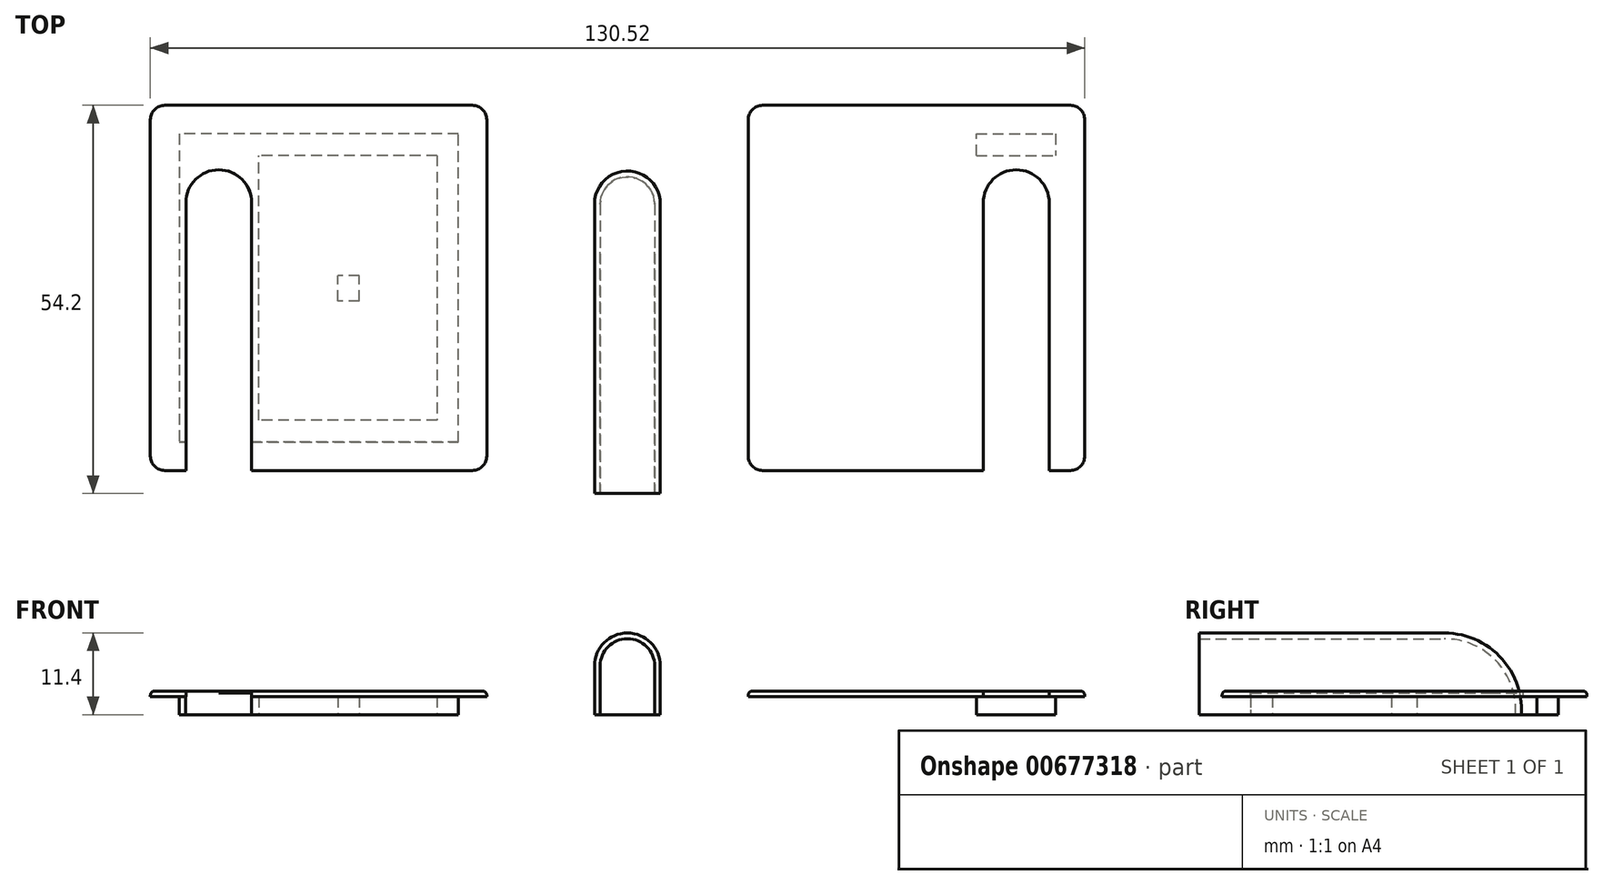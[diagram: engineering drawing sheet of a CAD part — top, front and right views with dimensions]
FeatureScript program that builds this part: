
annotation { "Feature Type Name" : "Feature", "Feature Type Description" : "" }
export const myFeature = defineFeature(function(context is Context, id is Id, definition is map)
    precondition{}
    {
        {
            var Q0;
            Q0=qCreatedBy(makeId("Top.planeOp"),FACE);
            var sketch = newSketch(context, id + "F0", { "sketchPlane" : qUnion([Q0])});
            skLineSegment(sketch, "E0.bottom", {"start": v(-22.21, 21.5) * mm, "end": v(-61.21, 21.5) * mm});
            skLineSegment(sketch, "E0.top", {"start": v(-22.21, -21.5) * mm, "end": v(-61.21, -21.5) * mm});
            skLineSegment(sketch, "E0.left", {"start": v(-22.21, 21.5) * mm, "end": v(-22.21, -21.5) * mm});
            skLineSegment(sketch, "E0.right", {"start": v(-61.21, 21.5) * mm, "end": v(-61.21, -21.5) * mm});
            skPoint(sketch, "E0.middle", {"position": v(-41.71, 0) * mm});
            skPoint(sketch, "E1.middle", {"position": v(-55.71, -10.56) * mm});
            skLineSegment(sketch, "E2", {"start": v(-50, 6.5) * mm, "end": v(0, 6.5) * mm, "construction": true});
            skLineSegment(sketch, "E3.0", {"start": v(0, 16.5) * mm, "end": v(-55.71, 16.5) * mm, "construction": true});
            skPoint(sketch, "E4.oppositeSnap0", {"position": v(-51.12, -5.81) * mm});
            skLineSegment(sketch, "E4.bottom", {"start": v(-60.31, -21.5) * mm, "end": v(-51.12, -21.5) * mm});
            skLineSegment(sketch, "E4.top", {"start": v(-60.28, 16.5) * mm, "end": v(-55.72, 16.5) * mm});
            skLineSegment(sketch, "E4.left", {"start": v(-60.31, -21.5) * mm, "end": v(-60.31, 11.9) * mm});
            skLineSegment(sketch, "E4.right", {"start": v(-51.12, -21.5) * mm, "end": v(-51.12, 11.9) * mm});
            skPoint(sketch, "E5.visualSharp", {"position": v(-51.12, 16.5) * mm});
            skArc(sketch, "E5.filletArc", {"start": v(-51.12, 11.9) * mm, "mid": v(-52.47, 15.15) * mm, "end": v(-55.72, 16.5) * mm});
            skArc(sketch, "E6.filletArc", {"start": v(-55.71, 16.5) * mm, "mid": v(-58.96, 15.15) * mm, "end": v(-60.31, 11.9) * mm});
            skLineSegment(sketch, "E7.0", {"start": v(-50.12, -21.5) * mm, "end": v(-50.12, 21.5) * mm});
            skLineSegment(sketch, "E8.0", {"start": v(-25.21, 18.5) * mm, "end": v(-61.21, 18.5) * mm});
            skLineSegment(sketch, "E8.1", {"start": v(-25.21, 18.5) * mm, "end": v(-25.21, -18.5) * mm});
            skLineSegment(sketch, "E8.2", {"start": v(-25.21, -18.5) * mm, "end": v(-61.21, -18.5) * mm});
            skLineSegment(sketch, "E9.bottom", {"start": v(-50.12, -1.8) * mm, "end": v(-25.21, -1.8) * mm});
            skLineSegment(sketch, "E9.top", {"start": v(-50.12, 1.7) * mm, "end": v(-25.21, 1.7) * mm});
            skLineSegment(sketch, "E9.left", {"start": v(-50.12, -1.8) * mm, "end": v(-50.12, 1.7) * mm});
            skLineSegment(sketch, "E9.right", {"start": v(-25.21, -1.8) * mm, "end": v(-25.21, 1.7) * mm});
            skLineSegment(sketch, "E10.bottom", {"start": v(-39.06, 18.5) * mm, "end": v(-36.06, 18.5) * mm});
            skLineSegment(sketch, "E10.top", {"start": v(-39.06, -18.5) * mm, "end": v(-36.06, -18.5) * mm});
            skLineSegment(sketch, "E10.left", {"start": v(-39.06, 18.5) * mm, "end": v(-39.06, -18.5) * mm});
            skLineSegment(sketch, "E10.right", {"start": v(-36.06, 18.5) * mm, "end": v(-36.06, -18.5) * mm});
            skSolve(sketch);
        }
        {
            var Q0;
            {var subQ5=sQuery(id+"F0.wireOp",EDGE,"DzNkT1zv-doSQ-e9RW-8Sh9-yqjNHehKiuAr.right");Q0=makeQuery(id+"F0.imprint","IMPRINT",FACE,{"disambiguationData":[TD([[makeQuery(id+"F0.imprint","IMPRINT",EDGE,{"derivedFrom":subQ5}),-1.0]])]});}
            var Q1;
            {var subQ0=sQuery(id+"F0.wireOp",EDGE,"DzNkT1zv-doSQ-e9RW-8Sh9-yqjNHehKiuAr.bottom");var subQ1=sQuery(id+"F0.wireOp",EDGE,"ce8b0b9d-27ce-47c4-a76a-4a8f725c700e.0");var subQ2=makeQuery(id+"F0.imprint","INTERSECT",VERTEX,{"derivedFrom":[subQ1,subQ0]});Q1=makeQuery(id+"F0.imprint","IMPRINT",FACE,{"disambiguationData":[TD([[makeQuery(id+"F0.imprint","IMPRINT",EDGE,{"disambiguationData":[TD([[subQ2,-1.0]])],"derivedFrom":subQ1}),-1.0]])]});}
            var Q2;
            {var subQ0=sQuery(id+"F0.wireOp",EDGE,"DzNkT1zv-doSQ-e9RW-8Sh9-yqjNHehKiuAr.bottom");var subQ1=sQuery(id+"F0.wireOp",EDGE,"0b0f2a42-a778-456e-be70-c8d79b466137.0");var subQ2=makeQuery(id+"F0.imprint","INTERSECT",VERTEX,{"derivedFrom":[subQ1,subQ0]});Q2=makeQuery(id+"F0.imprint","IMPRINT",FACE,{"disambiguationData":[TD([[makeQuery(id+"F0.imprint","IMPRINT",EDGE,{"disambiguationData":[TD([[subQ2,-1.0]])],"derivedFrom":subQ1}),1.0]])]});}
            var Q3;
            {var subQ0=sQuery(id+"F0.wireOp",EDGE,"DzNkT1zv-doSQ-e9RW-8Sh9-yqjNHehKiuAr.bottom");var subQ1=sQuery(id+"F0.wireOp",EDGE,"064e6164-91c3-4138-beae-8ed8de8ffb21.0");var subQ2=makeQuery(id+"F0.imprint","INTERSECT",VERTEX,{"derivedFrom":[subQ1,subQ0]});Q3=makeQuery(id+"F0.imprint","IMPRINT",FACE,{"disambiguationData":[TD([[makeQuery(id+"F0.imprint","IMPRINT",EDGE,{"disambiguationData":[TD([[subQ2,-1.0]])],"derivedFrom":subQ1}),1.0]])]});}
            var Q4;
            {var subQ0=sQuery(id+"F0.wireOp",EDGE,"064e6164-91c3-4138-beae-8ed8de8ffb21.0");var subQ1=sQuery(id+"F0.wireOp",EDGE,"dc2ccb20-c1df-4e72-943d-5ddd0a0731c1.2");var subQ2=makeQuery(id+"F0.imprint","INTERSECT",VERTEX,{"derivedFrom":[subQ1,subQ0]});Q4=makeQuery(id+"F0.imprint","IMPRINT",FACE,{"disambiguationData":[TD([[makeQuery(id+"F0.imprint","IMPRINT",EDGE,{"disambiguationData":[TD([[subQ2,1.0]])],"derivedFrom":subQ1}),1.0]])]});}
            var Q5;
            {var subQ0=sQuery(id+"F0.wireOp",EDGE,"ce8b0b9d-27ce-47c4-a76a-4a8f725c700e.0");var subQ1=sQuery(id+"F0.wireOp",EDGE,"dc2ccb20-c1df-4e72-943d-5ddd0a0731c1.2");var subQ2=makeQuery(id+"F0.imprint","INTERSECT",VERTEX,{"derivedFrom":[subQ1,subQ0]});Q5=makeQuery(id+"F0.imprint","IMPRINT",FACE,{"disambiguationData":[TD([[makeQuery(id+"F0.imprint","IMPRINT",EDGE,{"disambiguationData":[TD([[subQ2,-1.0]])],"derivedFrom":subQ1}),1.0]])]});}
            var Q6;
            {var subQ0=sQuery(id+"F0.wireOp",EDGE,"ce8b0b9d-27ce-47c4-a76a-4a8f725c700e.0");var subQ1=sQuery(id+"F0.wireOp",EDGE,"dc2ccb20-c1df-4e72-943d-5ddd0a0731c1.0");var subQ2=makeQuery(id+"F0.imprint","INTERSECT",VERTEX,{"derivedFrom":[subQ1,subQ0]});Q6=makeQuery(id+"F0.imprint","IMPRINT",FACE,{"disambiguationData":[TD([[makeQuery(id+"F0.imprint","IMPRINT",EDGE,{"disambiguationData":[TD([[subQ2,-1.0]])],"derivedFrom":subQ1}),-1.0]])]});}
            var Q7;
            {var subQ0=sQuery(id+"F0.wireOp",EDGE,"064e6164-91c3-4138-beae-8ed8de8ffb21.0");var subQ1=sQuery(id+"F0.wireOp",EDGE,"dc2ccb20-c1df-4e72-943d-5ddd0a0731c1.0");var subQ2=makeQuery(id+"F0.imprint","INTERSECT",VERTEX,{"derivedFrom":[subQ1,subQ0]});Q7=makeQuery(id+"F0.imprint","IMPRINT",FACE,{"disambiguationData":[TD([[makeQuery(id+"F0.imprint","IMPRINT",EDGE,{"disambiguationData":[TD([[subQ2,1.0]])],"derivedFrom":subQ1}),-1.0]])]});}
            var Q8;
            {var subQ20=sQuery(id+"F0.wireOp",EDGE,"E0.bottom");Q8=makeQuery(id+"F0.imprint","IMPRINT",FACE,{"disambiguationData":[TD([[makeQuery(id+"F0.imprint","IMPRINT",EDGE,{"derivedFrom":subQ20}),1.0]])]});}
            extrude(context, id + "F1", {"entities" : qUnion([Q0, Q1, Q2, Q3, Q4, Q5, Q6, Q7, Q8]), "depth" : 2.5 * mm, "offsetDistance" : 25 * mm});
        }
        {
            var Q0;
            Q0=makeQuery(id+"F1.opExtrude","CAP_FACE",FACE,{"disambiguationData":[OSD([sQuery(id+"F0.wireOp",EDGE,"E0.bottom"),sQuery(id+"F0.wireOp",EDGE,"E0.top"),sQuery(id+"F0.wireOp",EDGE,"E0.left"),sQuery(id+"F0.wireOp",EDGE,"E0.right"),sQuery(id+"F0.wireOp",EDGE,"dc2ccb20-c1df-4e72-943d-5ddd0a0731c1.0"),sQuery(id+"F0.wireOp",EDGE,"dc2ccb20-c1df-4e72-943d-5ddd0a0731c1.1"),sQuery(id+"F0.wireOp",EDGE,"dc2ccb20-c1df-4e72-943d-5ddd0a0731c1.2"),sQuery(id+"F0.wireOp",EDGE,"dc2ccb20-c1df-4e72-943d-5ddd0a0731c1.3"),sQuery(id+"F0.wireOp",EDGE,"064e6164-91c3-4138-beae-8ed8de8ffb21.0"),sQuery(id+"F0.wireOp",EDGE,"ce8b0b9d-27ce-47c4-a76a-4a8f725c700e.0"),sQuery(id+"F0.wireOp",EDGE,"0b0f2a42-a778-456e-be70-c8d79b466137.0"),sQuery(id+"F0.wireOp",EDGE,"c18b5a97-83d3-40bf-b302-a28a2e8d01a5.0"),sQuery(id+"F0.wireOp",EDGE,"DzNkT1zv-doSQ-e9RW-8Sh9-yqjNHehKiuAr.bottom"),sQuery(id+"F0.wireOp",EDGE,"DzNkT1zv-doSQ-e9RW-8Sh9-yqjNHehKiuAr.top"),sQuery(id+"F0.wireOp",EDGE,"56cf2d36-3c2d-4065-9a66-2b18e07928f5.0"),sQuery(id+"F0.wireOp",EDGE,"oqrG9gOV-pN6u-iuo7-ISGW-Ieqw6STCVA0x"),sQuery(id+"F0.wireOp",EDGE,"7Q4F9jyW-YGvi-0pui-QKdC-qTxHTYruCEjz")])],"isStart":false});
            var sketch = newSketch(context, id + "F2", { "sketchPlane" : qUnion([Q0])});
            skLineSegment(sketch, "E11.bottom", {"start": v(-20.26, -25.5) * mm, "end": v(-63.26, -25.5) * mm});
            skLineSegment(sketch, "E11.top", {"start": v(-20.26, 25.5) * mm, "end": v(-63.26, 25.5) * mm});
            skLineSegment(sketch, "E11.left", {"start": v(-18.26, -23.5) * mm, "end": v(-18.26, 23.5) * mm});
            skLineSegment(sketch, "E11.right", {"start": v(-65.26, -23.5) * mm, "end": v(-65.26, 23.5) * mm});
            skPoint(sketch, "E11.middle", {"position": v(-41.76, 0) * mm});
            skPoint(sketch, "E11.middle.positionSnap0", {"position": v(-41.76, -1.5) * mm});
            skPoint(sketch, "E11.centerSnap0", {"position": v(-41.76, -1.5) * mm});
            skPoint(sketch, "E12.visualSharp", {"position": v(-65.26, 25.5) * mm});
            skArc(sketch, "E12.filletArc", {"start": v(-63.26, 25.5) * mm, "mid": v(-64.68, 24.91) * mm, "end": v(-65.26, 23.5) * mm});
            skPoint(sketch, "E13.visualSharp", {"position": v(-18.26, 25.5) * mm});
            skArc(sketch, "E13.filletArc", {"start": v(-18.26, 23.5) * mm, "mid": v(-18.85, 24.91) * mm, "end": v(-20.26, 25.5) * mm});
            skPoint(sketch, "E14.visualSharp", {"position": v(-65.26, -25.5) * mm});
            skArc(sketch, "E14.filletArc", {"start": v(-65.26, -23.5) * mm, "mid": v(-64.68, -24.91) * mm, "end": v(-63.26, -25.5) * mm});
            skPoint(sketch, "E15.visualSharp", {"position": v(-18.26, -25.5) * mm});
            skArc(sketch, "E15.filletArc", {"start": v(-20.26, -25.5) * mm, "mid": v(-18.85, -24.91) * mm, "end": v(-18.26, -23.5) * mm});
            skLineSegment(sketch, "E16.bottom", {"start": v(-60.3, -25.5) * mm, "end": v(-51.1, -25.5) * mm});
            skLineSegment(sketch, "E16.top", {"start": v(-60.3, 11.9) * mm, "end": v(-51.1, 11.9) * mm});
            skLineSegment(sketch, "E16.left", {"start": v(-60.3, -25.5) * mm, "end": v(-60.3, 11.9) * mm});
            skLineSegment(sketch, "E16.right", {"start": v(-51.1, -25.5) * mm, "end": v(-51.1, 11.9) * mm});
            skArc(sketch, "E17", {"start": v(-51.1, 11.9) * mm, "mid": v(-55.7, 16.5) * mm, "end": v(-60.3, 11.9) * mm});
            skSolve(sketch);
        }
        {
            var Q0;
            Q0=makeQuery(id+"F2.imprint","IMPRINT",FACE,{"disambiguationData":[TD([[makeQuery(id+"F2.imprint","IMPRINT",EDGE,{"derivedFrom":sQuery(id+"F2.wireOp",EDGE,"E11.top")}),1.0]])]});
            var Q1;
            {var subQ5=sQuery(id+"F2.wireOp",EDGE,"E17");Q1=makeQuery(id+"F2.imprint","IMPRINT",FACE,{"disambiguationData":[TD([[makeQuery(id+"F2.imprint","IMPRINT",EDGE,{"derivedFrom":subQ5}),-1.0]])]});}
            var Q2;
            {var subQ0=sQuery(id+"F0.wireOp",EDGE,"0b0f2a42-a778-456e-be70-c8d79b466137.0");var subQ1=sQuery(id+"F0.wireOp",EDGE,"dc2ccb20-c1df-4e72-943d-5ddd0a0731c1.0");var subQ2=makeQuery(id+"F0.imprint","INTERSECT",VERTEX,{"derivedFrom":[subQ1,subQ0]});Q2=makeQuery(id+"F2.imprint","IMPRINT",FACE,{"disambiguationData":[TD([[makeQuery(id+"F2.imprint","IMPRINT",EDGE,{"derivedFrom":makeQuery(id+"F1.opExtrude","CAP_EDGE",EDGE,{"disambiguationData":[OSD([subQ1]),TDD([makeQuery(id+"F0.imprint","IMPRINT",EDGE,{"disambiguationData":[TD([[subQ2,1.0]])],"derivedFrom":subQ1})])],"isStart":false})}),-1.0]])]});}
            var Q3;
            {var subQ0=sQuery(id+"F0.wireOp",EDGE,"dc2ccb20-c1df-4e72-943d-5ddd0a0731c1.1");var subQ1=sQuery(id+"F0.wireOp",EDGE,"dc2ccb20-c1df-4e72-943d-5ddd0a0731c1.0");var subQ2=makeQuery(id+"F0.imprint","INTERSECT",VERTEX,{"derivedFrom":[subQ1,subQ0]});Q3=makeQuery(id+"F2.imprint","IMPRINT",FACE,{"disambiguationData":[TD([[makeQuery(id+"F2.imprint","IMPRINT",EDGE,{"derivedFrom":makeQuery(id+"F1.opExtrude","CAP_EDGE",EDGE,{"disambiguationData":[OSD([subQ1]),TDD([makeQuery(id+"F0.imprint","IMPRINT",EDGE,{"disambiguationData":[TD([[subQ2,-1.0]])],"derivedFrom":subQ1})])],"isStart":false})}),-1.0]])]});}
            var Q4;
            {var subQ0=sQuery(id+"F0.wireOp",EDGE,"dc2ccb20-c1df-4e72-943d-5ddd0a0731c1.2");var subQ1=sQuery(id+"F0.wireOp",EDGE,"dc2ccb20-c1df-4e72-943d-5ddd0a0731c1.1");var subQ2=makeQuery(id+"F0.imprint","INTERSECT",VERTEX,{"derivedFrom":[subQ1,subQ0]});Q4=makeQuery(id+"F2.imprint","IMPRINT",FACE,{"disambiguationData":[TD([[makeQuery(id+"F2.imprint","IMPRINT",EDGE,{"derivedFrom":makeQuery(id+"F1.opExtrude","CAP_EDGE",EDGE,{"disambiguationData":[OSD([subQ0]),TDD([makeQuery(id+"F0.imprint","IMPRINT",EDGE,{"disambiguationData":[TD([[subQ2,-1.0]])],"derivedFrom":subQ0})])],"isStart":false})}),1.0]])]});}
            var Q5;
            {var subQ0=sQuery(id+"F0.wireOp",EDGE,"0b0f2a42-a778-456e-be70-c8d79b466137.0");var subQ1=sQuery(id+"F0.wireOp",EDGE,"dc2ccb20-c1df-4e72-943d-5ddd0a0731c1.2");var subQ2=makeQuery(id+"F0.imprint","INTERSECT",VERTEX,{"derivedFrom":[subQ1,subQ0]});Q5=makeQuery(id+"F2.imprint","IMPRINT",FACE,{"disambiguationData":[TD([[makeQuery(id+"F2.imprint","IMPRINT",EDGE,{"derivedFrom":makeQuery(id+"F1.opExtrude","CAP_EDGE",EDGE,{"disambiguationData":[OSD([subQ1]),TDD([makeQuery(id+"F0.imprint","IMPRINT",EDGE,{"disambiguationData":[TD([[subQ2,1.0]])],"derivedFrom":subQ1})])],"isStart":false})}),1.0]])]});}
            var Q6;
            Q6=makeQuery(id+"F2.imprint","IMPRINT",FACE,{"disambiguationData":[TD([[makeQuery(id+"F2.imprint","IMPRINT",EDGE,{"derivedFrom":makeQuery(id+"F1.opExtrude","CAP_EDGE",EDGE,{"disambiguationData":[OSD([sQuery(id+"F0.wireOp",EDGE,"E0.bottom")])],"isStart":false})}),1.0]])]});
            extrude(context, id + "F3", {"entities" : qUnion([Q0, Q1, Q2, Q3, Q4, Q5, Q6]), "operationType" : NewBodyOperationType.ADD, "depth" : 0.8 * mm, "offsetDistance" : 25 * mm});
        }
        {
            var Q0;
            Q0=makeQuery(id+"F3.opExtrude","CAP_EDGE",EDGE,{"disambiguationData":[OSD([sQuery(id+"F2.wireOp",EDGE,"E11.left")])],"isStart":false});
            fillet(context, id + "F4", {"entities" : qUnion([Q0]), "radius" : 0.6 * mm, "tangentPropagation" : true, "allowEdgeOverflow" : false});
        }
        {
            var Q0;
            Q0=qCreatedBy(makeId("Top.planeOp"),FACE);
            var sketch = newSketch(context, id + "F5", { "sketchPlane" : qUnion([Q0])});
            skLineSegment(sketch, "E18", {"start": v(-3.22, 16.3) * mm, "end": v(-3.22, -28.7) * mm});
            skLineSegment(sketch, "E19", {"start": v(-3.22, -28.7) * mm, "end": v(-14.62, -28.7) * mm});
            skLineSegment(sketch, "E20", {"start": v(-14.62, -28.7) * mm, "end": v(-14.62, 5.56) * mm});
            skArc(sketch, "E21", {"start": v(-3.22, 16.3) * mm, "mid": v(-11.24, 13.39) * mm, "end": v(-14.62, 5.56) * mm});
            skSolve(sketch);
        }
        {
            var Q0;
            Q0 = qSketchRegion(id + "F5", true);
            extrude(context, id + "F6", {"entities" : qUnion([Q0]), "depth" : 9.2 * mm, "offsetDistance" : 25 * mm});
        }
        {
            var Q0;
            Q0=makeQuery(id+"F6.opExtrude","CAP_EDGE",EDGE,{"disambiguationData":[OSD([sQuery(id+"F5.wireOp",EDGE,"E21")])],"isStart":false});
            var Q1;
            Q1=makeQuery(id+"F6.opExtrude","CAP_EDGE",EDGE,{"disambiguationData":[OSD([sQuery(id+"F5.wireOp",EDGE,"E21")])],"isStart":true});
            fillet(context, id + "F7", {"entities" : qUnion([Q0, Q1]), "radius" : 4.6 * mm, "tangentPropagation" : true, "allowEdgeOverflow" : false});
        }
        {
            var Q0;
            Q0=makeQuery(id+"F6.opExtrude","SWEPT_FACE",FACE,{"disambiguationData":[OSD([sQuery(id+"F5.wireOp",EDGE,"E19")])]});
            var Q1;
            Q1=makeQuery(id+"F6.opExtrude","SWEPT_FACE",FACE,{"disambiguationData":[OSD([sQuery(id+"F5.wireOp",EDGE,"E18")])]});
            shell(context, id + "F8", {"entities" : qUnion([Q0, Q1]), "thickness" : 0.8 * mm});
        }
        {
            var Q0;
            Q0=makeQuery(id+"F6.opExtrude","CAP_EDGE",EDGE,{"disambiguationData":[OSD([sQuery(id+"F5.wireOp",EDGE,"E18")])],"isStart":true});
            cPoint(context, id + "F9", {"entities" : qUnion([Q0]), "parameter" : 0.5});
        }
        {
            var Q0;
            Q0=makeQuery(id+"F6.opExtrude","SWEPT_BODY",BODY,{"disambiguationData":[OSD([sQuery(id+"F5.wireOp",EDGE,"E18"),sQuery(id+"F5.wireOp",EDGE,"E19"),sQuery(id+"F5.wireOp",EDGE,"E20"),sQuery(id+"F5.wireOp",EDGE,"E21")])]});
            var Q1;
            Q1 = qCreatedBy(id + "F9" ,VERTEX);
            var Q2;
            Q2=makeQuery(id+"F6.opExtrude","CAP_EDGE",EDGE,{"disambiguationData":[OSD([sQuery(id+"F5.wireOp",EDGE,"E18")])],"isStart":true});
            transform(context, id + "F10", {"entities" : qUnion([Q0]), "transformType" : TransformType.ROTATION, "transformAxis" : qUnion([Q2]), "angle" : 90 * degree, "oppositeDirection" : true, "makeCopy" : false});
        }
        {
            var Q0;
            Q0=makeQuery(id+"F1.opExtrude","SWEPT_BODY",BODY,{"disambiguationData":[OSD([sQuery(id+"F0.wireOp",EDGE,"E0.bottom"),sQuery(id+"F0.wireOp",EDGE,"E0.top"),sQuery(id+"F0.wireOp",EDGE,"E0.left"),sQuery(id+"F0.wireOp",EDGE,"E0.right"),sQuery(id+"F0.wireOp",EDGE,"dc2ccb20-c1df-4e72-943d-5ddd0a0731c1.0"),sQuery(id+"F0.wireOp",EDGE,"dc2ccb20-c1df-4e72-943d-5ddd0a0731c1.1"),sQuery(id+"F0.wireOp",EDGE,"dc2ccb20-c1df-4e72-943d-5ddd0a0731c1.2"),sQuery(id+"F0.wireOp",EDGE,"dc2ccb20-c1df-4e72-943d-5ddd0a0731c1.3"),sQuery(id+"F0.wireOp",EDGE,"064e6164-91c3-4138-beae-8ed8de8ffb21.0"),sQuery(id+"F0.wireOp",EDGE,"ce8b0b9d-27ce-47c4-a76a-4a8f725c700e.0"),sQuery(id+"F0.wireOp",EDGE,"0b0f2a42-a778-456e-be70-c8d79b466137.0"),sQuery(id+"F0.wireOp",EDGE,"c18b5a97-83d3-40bf-b302-a28a2e8d01a5.0"),sQuery(id+"F0.wireOp",EDGE,"DzNkT1zv-doSQ-e9RW-8Sh9-yqjNHehKiuAr.bottom"),sQuery(id+"F0.wireOp",EDGE,"DzNkT1zv-doSQ-e9RW-8Sh9-yqjNHehKiuAr.top"),sQuery(id+"F0.wireOp",EDGE,"56cf2d36-3c2d-4065-9a66-2b18e07928f5.0"),sQuery(id+"F0.wireOp",EDGE,"oqrG9gOV-pN6u-iuo7-ISGW-Ieqw6STCVA0x"),sQuery(id+"F0.wireOp",EDGE,"7Q4F9jyW-YGvi-0pui-QKdC-qTxHTYruCEjz")])]});
            var Q1;
            Q1=qCreatedBy(makeId("Right.planeOp"),FACE);
            mirror(context, id + "F11", {"entities" : qUnion([Q0]), "mirrorPlane" : qUnion([Q1])});
        }
        {
            var Q0;
            {var subQ0=sQuery(id+"F0.wireOp",EDGE,"E0.right");var subQ1=sQuery(id+"F0.wireOp",EDGE,"E0.bottom");var subQ2=makeQuery(id+"F0.imprint","INTERSECT",VERTEX,{"derivedFrom":[subQ1,subQ0]});Q0=makeQuery(id+"F0.imprint","IMPRINT",FACE,{"disambiguationData":[TD([[makeQuery(id+"F0.imprint","IMPRINT",EDGE,{"disambiguationData":[TD([[subQ2,1.0]])],"derivedFrom":subQ1}),1.0]])]});}
            var Q1;
            {var subQ14=sQuery(id+"F0.wireOp",EDGE,"E5.filletArc");Q1=makeQuery(id+"F0.imprint","IMPRINT",FACE,{"disambiguationData":[TD([[makeQuery(id+"F0.imprint","IMPRINT",EDGE,{"derivedFrom":subQ14}),-1.0]])]});}
            var Q2;
            {var subQ6=sQuery(id+"F0.wireOp",EDGE,"E0.left");Q2=makeQuery(id+"F0.imprint","IMPRINT",FACE,{"disambiguationData":[TD([[makeQuery(id+"F0.imprint","IMPRINT",EDGE,{"derivedFrom":subQ6}),-1.0]])]});}
            var Q3;
            {var subQ5=sQuery(id+"F0.wireOp",EDGE,"E10.bottom");Q3=makeQuery(id+"F0.imprint","IMPRINT",FACE,{"disambiguationData":[TD([[makeQuery(id+"F0.imprint","IMPRINT",EDGE,{"derivedFrom":subQ5}),-1.0]])]});}
            var Q4;
            {var subQ0=sQuery(id+"F0.wireOp",EDGE,"E9.right");Q4=makeQuery(id+"F0.imprint","IMPRINT",FACE,{"disambiguationData":[TD([[makeQuery(id+"F0.imprint","IMPRINT",EDGE,{"derivedFrom":subQ0}),1.0]])]});}
            var Q5;
            {var subQ0=sQuery(id+"F0.wireOp",EDGE,"E9.left");Q5=makeQuery(id+"F0.imprint","IMPRINT",FACE,{"disambiguationData":[TD([[makeQuery(id+"F0.imprint","IMPRINT",EDGE,{"derivedFrom":subQ0}),-1.0]])]});}
            var Q6;
            {var subQ5=sQuery(id+"F0.wireOp",EDGE,"E10.top");Q6=makeQuery(id+"F0.imprint","IMPRINT",FACE,{"disambiguationData":[TD([[makeQuery(id+"F0.imprint","IMPRINT",EDGE,{"derivedFrom":subQ5}),1.0]])]});}
            var Q7;
            {var subQ0=sQuery(id+"F0.wireOp",EDGE,"E10.left");var subQ1=sQuery(id+"F0.wireOp",EDGE,"E9.bottom");var subQ2=makeQuery(id+"F0.imprint","INTERSECT",VERTEX,{"derivedFrom":[subQ1,subQ0]});Q7=makeQuery(id+"F0.imprint","IMPRINT",FACE,{"disambiguationData":[TD([[makeQuery(id+"F0.imprint","IMPRINT",EDGE,{"disambiguationData":[TD([[subQ2,-1.0]])],"derivedFrom":subQ1}),1.0]])]});}
            var Q8;
            {var subQ1=sQuery(id+"F0.wireOp",EDGE,"E0.top");var subQ3=sQuery(id+"F0.wireOp",EDGE,"E7.0");var subQ4=makeQuery(id+"F0.imprint","INTERSECT",VERTEX,{"derivedFrom":[subQ1,subQ3]});Q8=makeQuery(id+"F0.imprint","IMPRINT",FACE,{"disambiguationData":[TD([[makeQuery(id+"F0.imprint","IMPRINT",EDGE,{"disambiguationData":[TD([[subQ4,-1.0]])],"derivedFrom":subQ3}),1.0]])]});}
            var Q9;
            {var subQ0=sQuery(id+"F0.wireOp",EDGE,"E0.right");var subQ1=sQuery(id+"F0.wireOp",EDGE,"E0.top");var subQ2=makeQuery(id+"F0.imprint","INTERSECT",VERTEX,{"derivedFrom":[subQ1,subQ0]});Q9=makeQuery(id+"F0.imprint","IMPRINT",FACE,{"disambiguationData":[TD([[makeQuery(id+"F0.imprint","IMPRINT",EDGE,{"disambiguationData":[TD([[subQ2,1.0]])],"derivedFrom":subQ0}),1.0]])]});}
            extrude(context, id + "F12", {"entities" : qUnion([Q0, Q1, Q2, Q3, Q4, Q5, Q6, Q7, Q8, Q9]), "operationType" : NewBodyOperationType.ADD, "depth" : 3 * mm, "offsetDistance" : 25 * mm});
        }
    });
